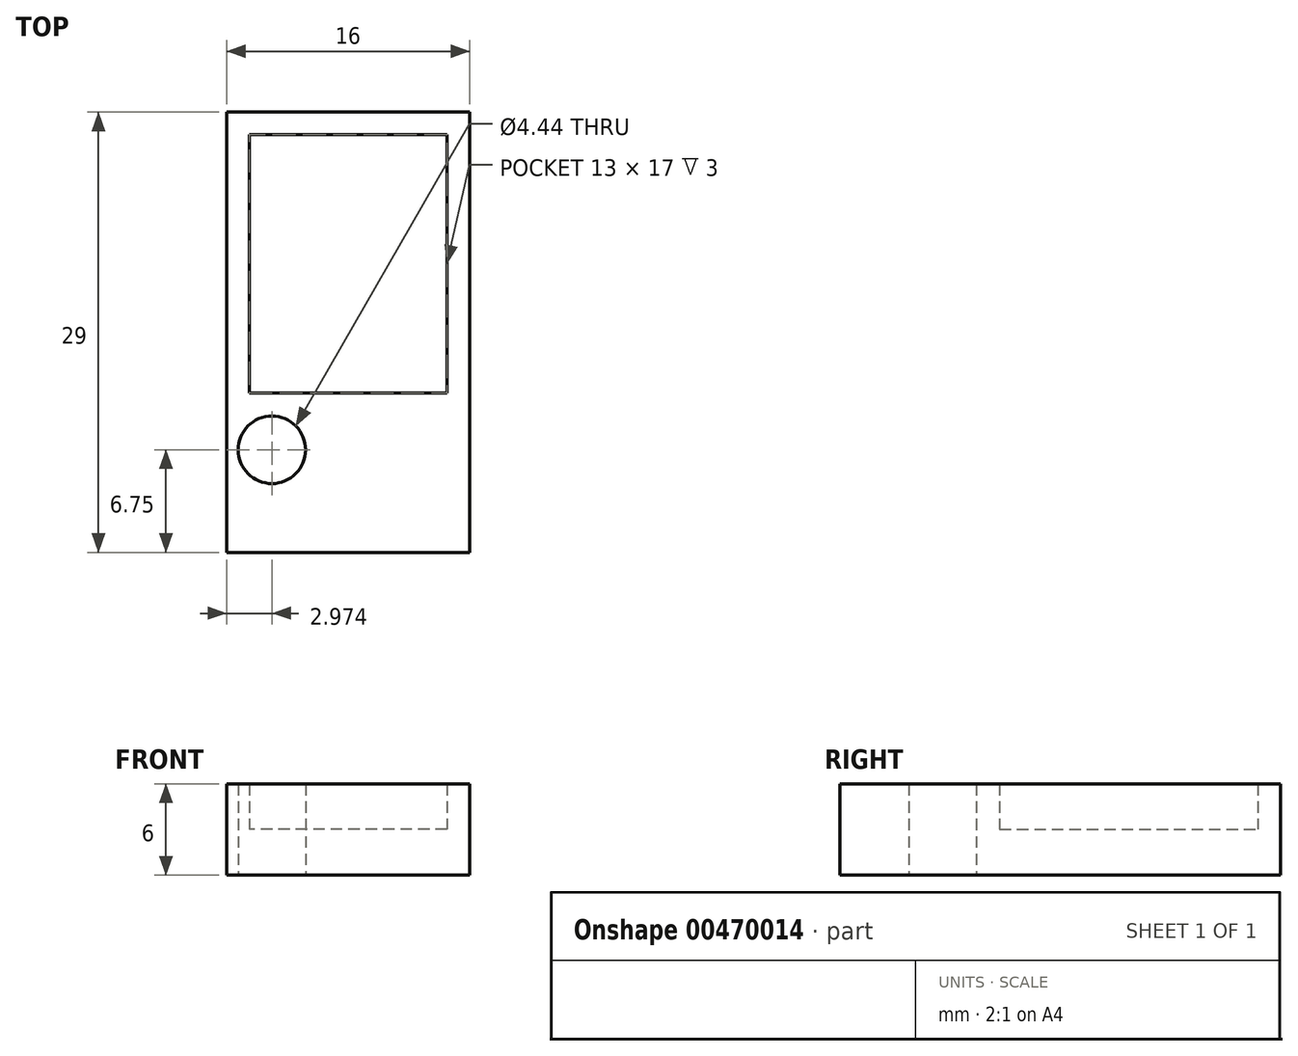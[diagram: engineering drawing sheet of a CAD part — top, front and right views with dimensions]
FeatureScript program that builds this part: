
annotation { "Feature Type Name" : "Feature", "Feature Type Description" : "" }
export const myFeature = defineFeature(function(context is Context, id is Id, definition is map)
    precondition{}
    {
        {
            var Q0;
            Q0=qCreatedBy(makeId("Top.planeOp"),FACE);
            var sketch = newSketch(context, id + "F0", { "sketchPlane" : qUnion([Q0])});
            skLineSegment(sketch, "E0.bottom", {"start": v(8, -14.5) * mm, "end": v(-8, -14.5) * mm});
            skLineSegment(sketch, "E0.top", {"start": v(8, 14.5) * mm, "end": v(-8, 14.5) * mm});
            skLineSegment(sketch, "E0.left", {"start": v(8, -14.5) * mm, "end": v(8, 14.5) * mm});
            skLineSegment(sketch, "E0.right", {"start": v(-8, -14.5) * mm, "end": v(-8, 14.5) * mm});
            skPoint(sketch, "E0.middle", {"position": v(0, 0) * mm});
            skLineSegment(sketch, "E1.bottom", {"start": v(5.03, -10) * mm, "end": v(-5.03, -10) * mm});
            skLineSegment(sketch, "E1.top", {"start": v(5.03, -5.5) * mm, "end": v(-5.03, -5.5) * mm});
            skLineSegment(sketch, "E1.left", {"start": v(5.03, -10) * mm, "end": v(5.03, -5.5) * mm});
            skLineSegment(sketch, "E1.right", {"start": v(-5.03, -10) * mm, "end": v(-5.03, -5.5) * mm});
            skPoint(sketch, "E1.middle", {"position": v(0, -7.75) * mm});
            skCircle(sketch, "E2", {"center": v(-5.03, -7.75) * mm, "radius": 2.22 * mm});
            skCircle(sketch, "E3", {"center": v(5.03, -7.75) * mm, "radius": 2.25 * mm});
            skLineSegment(sketch, "E4.bottom", {"start": v(6.5, -4) * mm, "end": v(-6.5, -4) * mm});
            skLineSegment(sketch, "E4.top", {"start": v(6.5, 13) * mm, "end": v(-6.5, 13) * mm});
            skLineSegment(sketch, "E4.left", {"start": v(6.5, -4) * mm, "end": v(6.5, 13) * mm});
            skLineSegment(sketch, "E4.right", {"start": v(-6.5, -4) * mm, "end": v(-6.5, 13) * mm});
            skPoint(sketch, "E4.middle", {"position": v(0, 4.5) * mm});
            skSolve(sketch);
        }
        {
            var Q0;
            Q0 = qSketchRegion(id + "F0", true);
            extrude(context, id + "F1", {"entities" : qUnion([Q0]), "depth" : 2 * mm, "offsetDistance" : 25 * mm});
        }
        {
            var Q0;
            {var subQ0=sQuery(id+"F0.wireOp",EDGE,"E2");var subQ1=sQuery(id+"F0.wireOp",EDGE,"E1.right");var subQ2=makeQuery(id+"F0.imprint","INTERSECT",VERTEX,{"disambiguationData":[OD(0.0)],"derivedFrom":[subQ1,subQ0]});Q0=makeQuery(id+"F0.imprint","IMPRINT",FACE,{"disambiguationData":[TD([[makeQuery(id+"F0.imprint","IMPRINT",EDGE,{"disambiguationData":[TD([[subQ2,-1.0]])],"derivedFrom":subQ1}),-1.0]])]});}
            var Q1;
            {var subQ0=sQuery(id+"F0.wireOp",EDGE,"E2");var subQ1=sQuery(id+"F0.wireOp",EDGE,"E1.right");var subQ2=makeQuery(id+"F0.imprint","INTERSECT",VERTEX,{"disambiguationData":[OD(0.0)],"derivedFrom":[subQ1,subQ0]});Q1=makeQuery(id+"F0.imprint","IMPRINT",FACE,{"disambiguationData":[TD([[makeQuery(id+"F0.imprint","IMPRINT",EDGE,{"disambiguationData":[TD([[subQ2,-1.0]])],"derivedFrom":subQ1}),1.0]])]});}
            var Q2;
            {var subQ0=sQuery(id+"F0.wireOp",EDGE,"E1.left");Q2=makeQuery(id+"F0.imprint","IMPRINT",FACE,{"disambiguationData":[TD([[makeQuery(id+"F0.imprint","IMPRINT",EDGE,{"derivedFrom":subQ0}),1.0]])]});}
            var Q3;
            {var subQ0=sQuery(id+"F0.wireOp",EDGE,"E1.left");Q3=makeQuery(id+"F0.imprint","IMPRINT",FACE,{"disambiguationData":[TD([[makeQuery(id+"F0.imprint","IMPRINT",EDGE,{"derivedFrom":subQ0}),-1.0]])]});}
            var Q4;
            {var subQ1=sQuery(id+"F0.wireOp",EDGE,"E1.bottom");Q4=makeQuery(id+"F0.imprint","IMPRINT",FACE,{"disambiguationData":[TD([[makeQuery(id+"F0.imprint","IMPRINT",EDGE,{"derivedFrom":subQ1}),-1.0]])]});}
            extrude(context, id + "F2", {"entities" : qUnion([Q0, Q1, Q2, Q3, Q4]), "operationType" : NewBodyOperationType.ADD, "depth" : 6 * mm, "offsetDistance" : 25 * mm});
        }
        {
            var Q0;
            Q0=makeQuery(id+"F0.imprint","IMPRINT",FACE,{"disambiguationData":[TD([[makeQuery(id+"F0.imprint","IMPRINT",EDGE,{"derivedFrom":sQuery(id+"F0.wireOp",EDGE,"E4.bottom")}),-1.0]])]});
            extrude(context, id + "F3", {"entities" : qUnion([Q0]), "operationType" : NewBodyOperationType.ADD, "depth" : 3 * mm, "offsetDistance" : 25 * mm});
        }
    });
